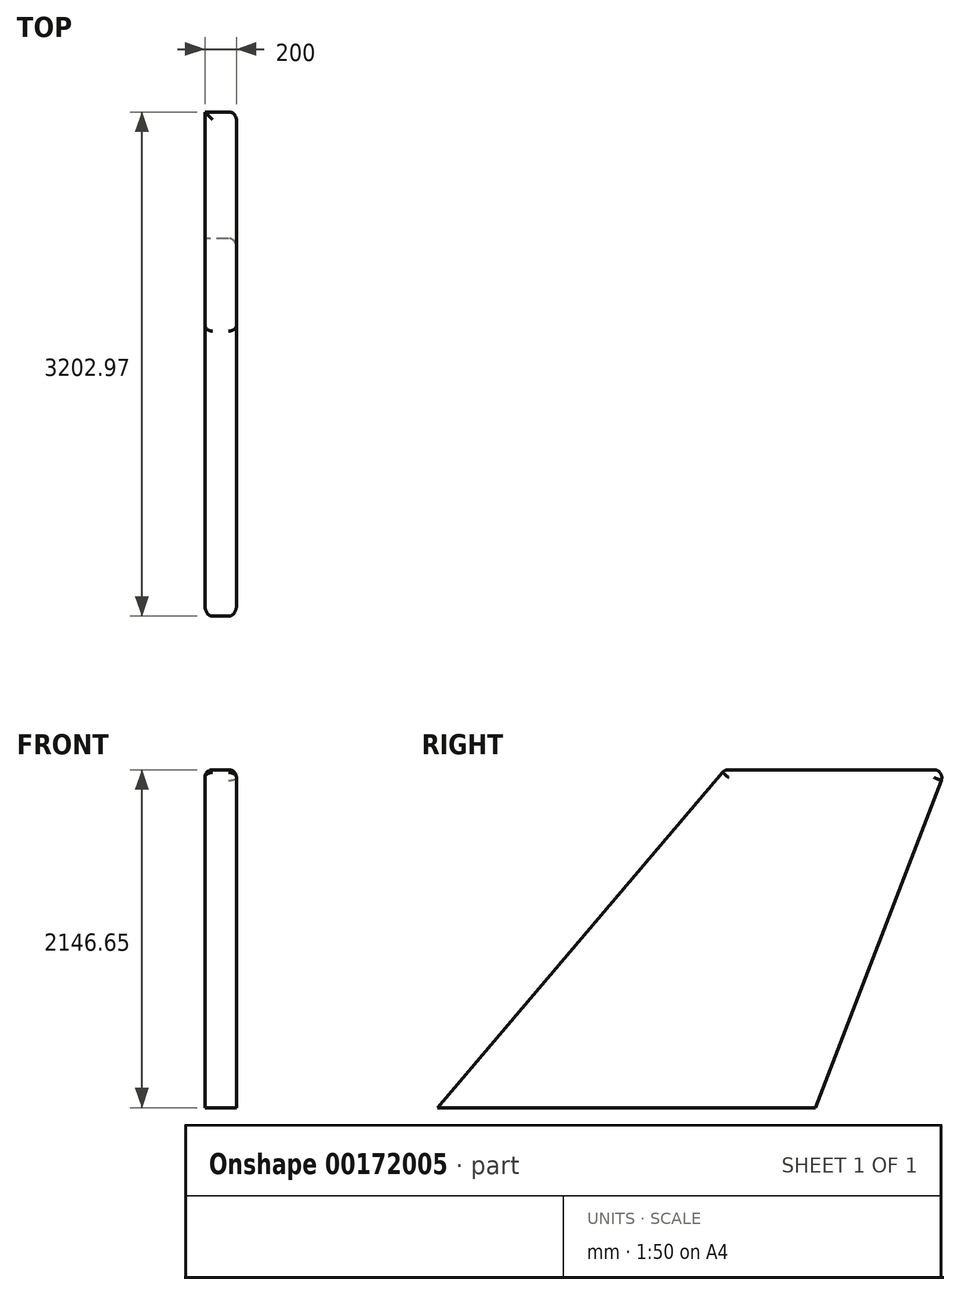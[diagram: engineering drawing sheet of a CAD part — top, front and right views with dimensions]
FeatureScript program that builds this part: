
annotation { "Feature Type Name" : "Feature", "Feature Type Description" : "" }
export const myFeature = defineFeature(function(context is Context, id is Id, definition is map)
    precondition{}
    {
        {
            var Q0;
            Q0=qCreatedBy(makeId("Right.planeOp"),FACE);
            var sketch = newSketch(context, id + "F0", { "sketchPlane" : qUnion([Q0])});
            skLineSegment(sketch, "E0", {"start": v(-1318.74, 0) * mm, "end": v(1081.26, 0) * mm});
            skLineSegment(sketch, "E1", {"start": v(1081.26, 0) * mm, "end": v(1907.04, 2146.65) * mm});
            skLineSegment(sketch, "E2", {"start": v(1907.04, 2146.65) * mm, "end": v(507.04, 2146.65) * mm});
            skLineSegment(sketch, "E3", {"start": v(507.04, 2146.65) * mm, "end": v(-1318.74, 0) * mm});
            skSolve(sketch);
        }
        {
            var Q0;
            Q0=qCreatedBy(makeId("Front.planeOp"),FACE);
            var sketch = newSketch(context, id + "F1", { "sketchPlane" : qUnion([Q0])});
            skSolve(sketch);
        }
        {
            var Q0;
            Q0 = qSketchRegion(id + "F1", true);
            var Q1;
            Q1=makeQuery(id+"F0.imprint","IMPRINT",FACE,{"disambiguationData":[TD([[makeQuery(id+"F0.imprint","IMPRINT",EDGE,{"derivedFrom":sQuery(id+"F0.wireOp",EDGE,"E0")}),1.0]])]});
            extrude(context, id + "F2", {"entities" : qUnion([Q0, Q1]), "endBound" : BoundingType.SYMMETRIC, "depth" : 200 * mm});
        }
        {
            var Q0;
            Q0=makeQuery(id+"F2.opExtrude","CAP_EDGE",EDGE,{"disambiguationData":[OSD([sQuery(id+"F0.wireOp",EDGE,"E3")])],"isStart":true});
            var Q1;
            Q1=makeQuery(id+"F2.opExtrude","CAP_EDGE",EDGE,{"disambiguationData":[OSD([sQuery(id+"F0.wireOp",EDGE,"E3")])],"isStart":false});
            var Q2;
            Q2=makeQuery(id+"F2.opExtrude","CAP_EDGE",EDGE,{"disambiguationData":[OSD([sQuery(id+"F0.wireOp",EDGE,"E1")])],"isStart":false});
            fillet(context, id + "F3", {"entities" : qUnion([Q0, Q1, Q2]), "radius" : 50 * mm, "tangentPropagation" : true, "allowEdgeOverflow" : false});
        }
        {
            var Q0;
            Q0=makeQuery(id+"F2.opExtrude","CAP_EDGE",EDGE,{"disambiguationData":[OSD([sQuery(id+"F0.wireOp",EDGE,"E2")])],"isStart":false});
            var Q1;
            Q1=makeQuery(id+"F2.opExtrude","CAP_EDGE",EDGE,{"disambiguationData":[OSD([sQuery(id+"F0.wireOp",EDGE,"E2")])],"isStart":true});
            fillet(context, id + "F4", {"entities" : qUnion([Q0, Q1]), "radius" : 50 * mm, "tangentPropagation" : true, "allowEdgeOverflow" : false});
        }
    });
